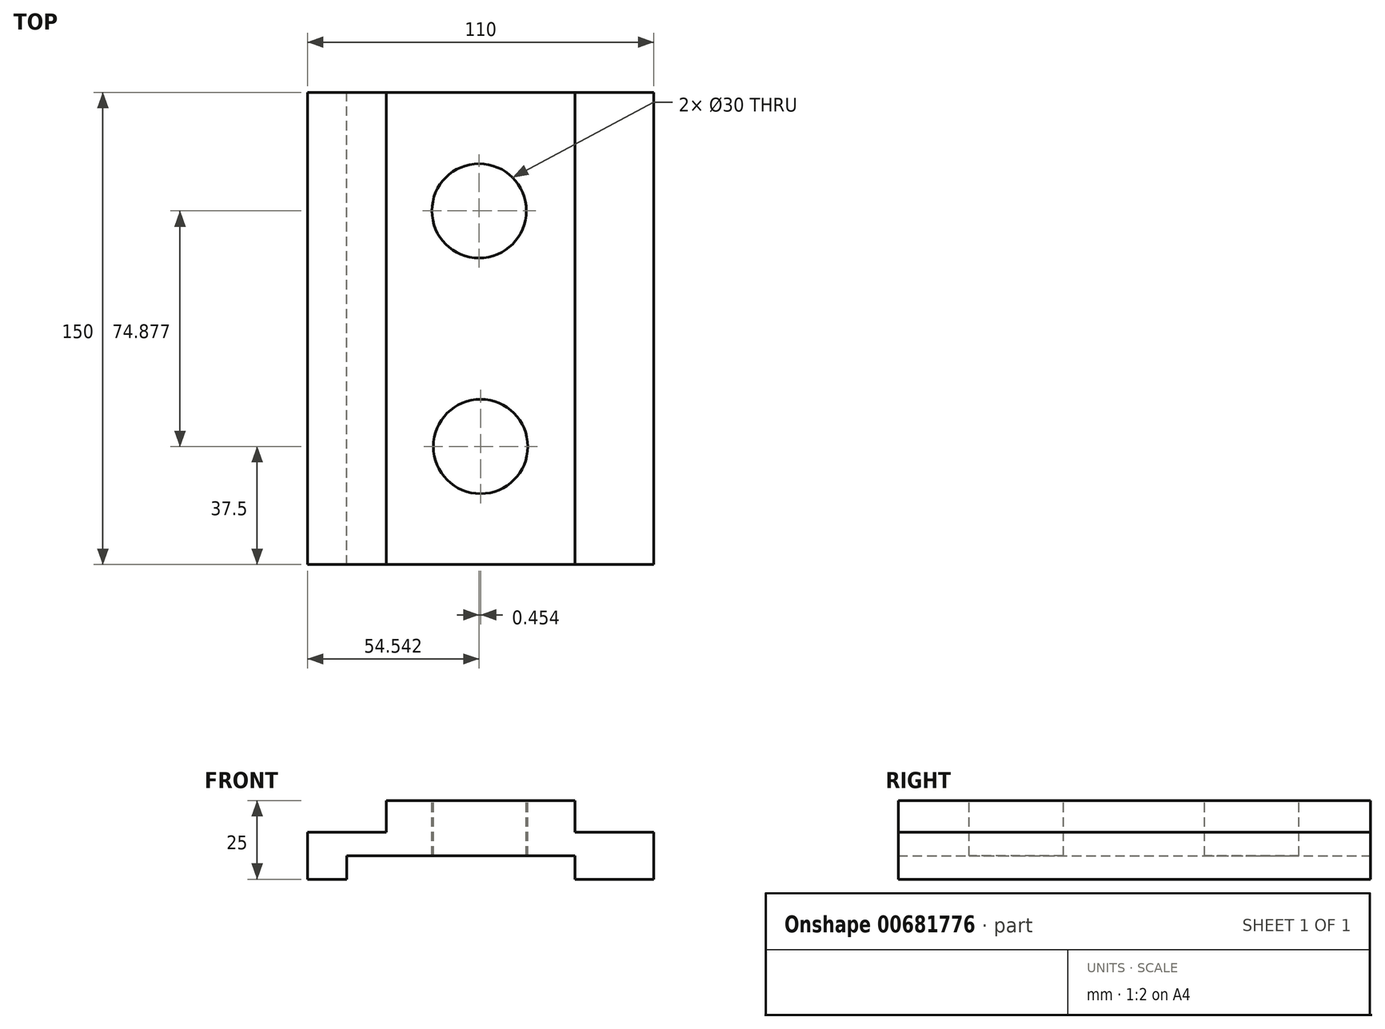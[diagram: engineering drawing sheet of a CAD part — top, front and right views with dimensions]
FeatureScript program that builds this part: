
annotation { "Feature Type Name" : "Feature", "Feature Type Description" : "" }
export const myFeature = defineFeature(function(context is Context, id is Id, definition is map)
    precondition{}
    {
        {
            var Q0;
            Q0=qCreatedBy(makeId("Front.planeOp"),FACE);
            var sketch = newSketch(context, id + "F0", { "sketchPlane" : qUnion([Q0])});
            skLineSegment(sketch, "E0.bottom", {"start": v(-54.4, -15) * mm, "end": v(-41.9, -15) * mm});
            skLineSegment(sketch, "E0.top", {"start": v(-54.4, 0) * mm, "end": v(-29.4, 0) * mm});
            skLineSegment(sketch, "E0.left", {"start": v(-54.4, -15) * mm, "end": v(-54.4, 0) * mm});
            skLineSegment(sketch, "E0.right", {"start": v(55.6, -15) * mm, "end": v(55.6, 0) * mm});
            skLineSegment(sketch, "E1.top", {"start": v(-29.4, 10) * mm, "end": v(30.6, 10) * mm});
            skLineSegment(sketch, "E1.left", {"start": v(-29.4, 0) * mm, "end": v(-29.4, 10) * mm});
            skLineSegment(sketch, "E1.right", {"start": v(30.6, 0) * mm, "end": v(30.6, 10) * mm});
            skLineSegment(sketch, "E2.top", {"start": v(-41.9, -7.5) * mm, "end": v(30.6, -7.5) * mm});
            skLineSegment(sketch, "E2.left", {"start": v(-41.9, -15) * mm, "end": v(-41.9, -7.5) * mm});
            skLineSegment(sketch, "E2.right", {"start": v(30.6, -15) * mm, "end": v(30.6, -7.5) * mm});
            skLineSegment(sketch, "E3.trimOffspring", {"start": v(30.6, -15) * mm, "end": v(55.6, -15) * mm});
            skLineSegment(sketch, "E4.trimOffspring", {"start": v(30.6, 0) * mm, "end": v(55.6, 0) * mm});
            skSolve(sketch);
        }
        {
            var Q0;
            Q0 = qSketchRegion(id + "F0", true);
            extrude(context, id + "F1", {"entities" : qUnion([Q0]), "depth" : 150 * mm, "offsetDistance" : 25 * mm});
        }
        {
            var Q0;
            Q0=makeQuery(id+"F1.opExtrude","SWEPT_FACE",FACE,{"disambiguationData":[OSD([sQuery(id+"F0.wireOp",EDGE,"E1.top")])]});
            var sketch = newSketch(context, id + "F2", { "sketchPlane" : qUnion([Q0])});
            skLineSegment(sketch, "E5", {"start": v(0, 0) * mm, "end": v(0.6, -150) * mm});
            skLineSegment(sketch, "E6", {"start": v(-29.4, -37.74) * mm, "end": v(30.6, -37.5) * mm});
            skLineSegment(sketch, "E7", {"start": v(-29.4, -112.5) * mm, "end": v(30.6, -112.5) * mm});
            skPoint(sketch, "E8.orphan", {"position": v(-29.4, -75) * mm});
            skPoint(sketch, "E9.end.orphan", {"position": v(30.6, -75) * mm});
            skCircle(sketch, "E10", {"center": v(0.15, -37.62) * mm, "radius": 15 * mm});
            skCircle(sketch, "E11", {"center": v(0.6, -112.5) * mm, "radius": 15 * mm});
            skSolve(sketch);
        }
        {
            var Q0;
            Q0 = qSketchRegion(id + "F2", true);
            extrude(context, id + "F3", {"entities" : qUnion([Q0]), "operationType" : NewBodyOperationType.REMOVE, "oppositeDirection" : true, "depth" : 50 * mm, "offsetDistance" : 25 * mm});
        }
    });
